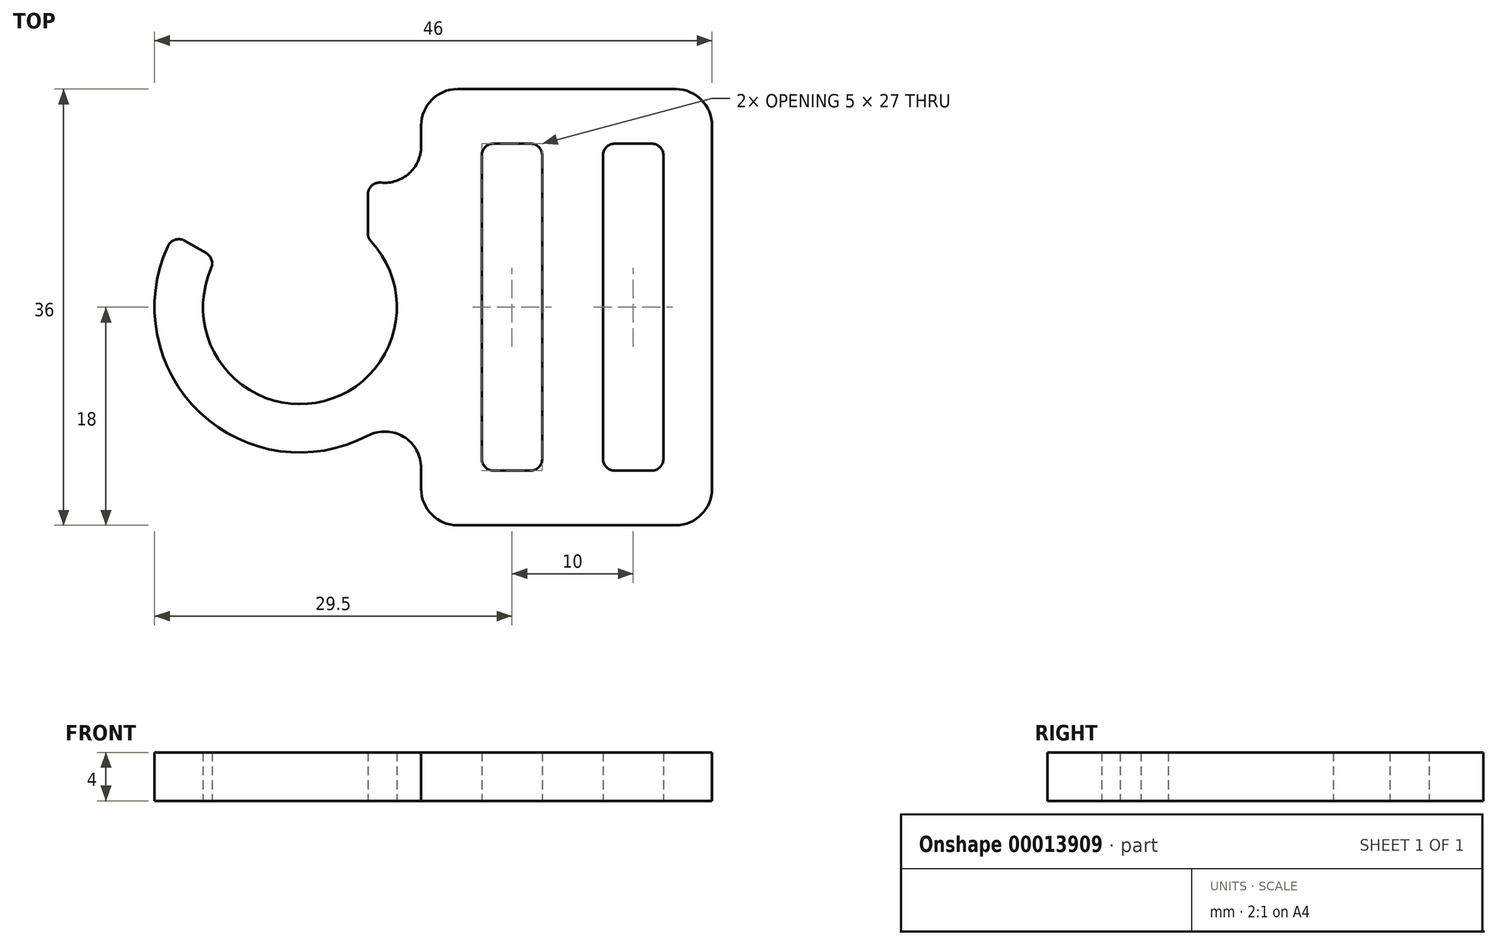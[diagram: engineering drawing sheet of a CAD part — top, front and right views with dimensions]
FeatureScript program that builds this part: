
annotation { "Feature Type Name" : "Feature", "Feature Type Description" : "" }
export const myFeature = defineFeature(function(context is Context, id is Id, definition is map)
    precondition{}
    {
        {
            var Q0;
            Q0=qCreatedBy(makeId("Top.planeOp"),FACE);
            var sketch = newSketch(context, id + "F0", { "sketchPlane" : qUnion([Q0])});
            skArc(sketch, "E0", {"start": v(-10.9, 5.03) * mm, "mid": v(-8.26, -8.7) * mm, "end": v(5.6, -10.61) * mm});
            skLineSegment(sketch, "E1.bottom", {"start": v(13, 18) * mm, "end": v(31, 18) * mm});
            skLineSegment(sketch, "E1.top", {"start": v(13, -18) * mm, "end": v(31, -18) * mm});
            skLineSegment(sketch, "E1.left", {"start": v(10, 15) * mm, "end": v(10, 13.27) * mm});
            skLineSegment(sketch, "E1.right", {"start": v(34, 15) * mm, "end": v(34, -15) * mm});
            skArc(sketch, "E2", {"start": v(-7.33, 3.2) * mm, "mid": v(1.34, -7.89) * mm, "end": v(5.87, 5.44) * mm});
            skLineSegment(sketch, "E3.trimOffspring", {"start": v(10, -13.27) * mm, "end": v(10, -15) * mm});
            skLineSegment(sketch, "E4.bottom", {"start": v(16, 13.5) * mm, "end": v(19, 13.5) * mm});
            skLineSegment(sketch, "E4.top", {"start": v(16, -13.5) * mm, "end": v(19, -13.5) * mm});
            skLineSegment(sketch, "E4.left", {"start": v(15, 12.5) * mm, "end": v(15, -12.5) * mm});
            skLineSegment(sketch, "E4.right", {"start": v(20, 12.5) * mm, "end": v(20, -12.5) * mm});
            skLineSegment(sketch, "E5.bottom", {"start": v(26, 13.5) * mm, "end": v(29, 13.5) * mm});
            skLineSegment(sketch, "E5.top", {"start": v(26, -13.5) * mm, "end": v(29, -13.5) * mm});
            skLineSegment(sketch, "E5.left", {"start": v(25, 12.5) * mm, "end": v(25, -12.5) * mm});
            skLineSegment(sketch, "E5.right", {"start": v(30, 12.5) * mm, "end": v(30, -12.5) * mm});
            skLineSegment(sketch, "E6", {"start": v(0, 0) * mm, "end": v(34, 0) * mm, "construction": true});
            skPoint(sketch, "E7", {"position": v(25, 0) * mm});
            skPoint(sketch, "E8.visualSharp", {"position": v(10, 6.63) * mm});
            skArc(sketch, "E8.filletArc", {"start": v(6.7, 10.28) * mm, "mid": v(9.01, 11.04) * mm, "end": v(10, 13.27) * mm});
            skPoint(sketch, "E9.visualSharp", {"position": v(10, -6.63) * mm});
            skArc(sketch, "E9.filletArc", {"start": v(10, -13.27) * mm, "mid": v(8.55, -10.7) * mm, "end": v(5.6, -10.61) * mm});
            skPoint(sketch, "E10.visualSharp", {"position": v(10, -18) * mm});
            skArc(sketch, "E10.filletArc", {"start": v(10, -15) * mm, "mid": v(10.88, -17.12) * mm, "end": v(13, -18) * mm});
            skPoint(sketch, "E11.visualSharp", {"position": v(34, -18) * mm});
            skArc(sketch, "E11.filletArc", {"start": v(31, -18) * mm, "mid": v(33.12, -17.12) * mm, "end": v(34, -15) * mm});
            skPoint(sketch, "E12.visualSharp", {"position": v(34, 18) * mm});
            skArc(sketch, "E12.filletArc", {"start": v(34, 15) * mm, "mid": v(33.12, 17.12) * mm, "end": v(31, 18) * mm});
            skPoint(sketch, "E13.visualSharp", {"position": v(10, 18) * mm});
            skArc(sketch, "E13.filletArc", {"start": v(13, 18) * mm, "mid": v(10.88, 17.12) * mm, "end": v(10, 15) * mm});
            skPoint(sketch, "E14.visualSharp", {"position": v(15, 13.5) * mm});
            skArc(sketch, "E14.filletArc", {"start": v(16, 13.5) * mm, "mid": v(15.3, 13.2) * mm, "end": v(15, 12.5) * mm});
            skPoint(sketch, "E15.visualSharp", {"position": v(20, 13.5) * mm});
            skArc(sketch, "E15.filletArc", {"start": v(20, 12.5) * mm, "mid": v(19.7, 13.2) * mm, "end": v(19, 13.5) * mm});
            skPoint(sketch, "E16.visualSharp", {"position": v(25, 13.5) * mm});
            skArc(sketch, "E16.filletArc", {"start": v(26, 13.5) * mm, "mid": v(25.3, 13.2) * mm, "end": v(25, 12.5) * mm});
            skPoint(sketch, "E17.visualSharp", {"position": v(30, 13.5) * mm});
            skArc(sketch, "E17.filletArc", {"start": v(30, 12.5) * mm, "mid": v(29.7, 13.2) * mm, "end": v(29, 13.5) * mm});
            skPoint(sketch, "E18.visualSharp", {"position": v(30, -13.5) * mm});
            skArc(sketch, "E18.filletArc", {"start": v(29, -13.5) * mm, "mid": v(29.7, -13.2) * mm, "end": v(30, -12.5) * mm});
            skPoint(sketch, "E19.visualSharp", {"position": v(25, -13.5) * mm});
            skArc(sketch, "E19.filletArc", {"start": v(25, -12.5) * mm, "mid": v(25.3, -13.2) * mm, "end": v(26, -13.5) * mm});
            skPoint(sketch, "E20.visualSharp", {"position": v(15, -13.5) * mm});
            skArc(sketch, "E20.filletArc", {"start": v(15, -12.5) * mm, "mid": v(15.3, -13.2) * mm, "end": v(16, -13.5) * mm});
            skPoint(sketch, "E21.visualSharp", {"position": v(20, -13.5) * mm});
            skArc(sketch, "E21.filletArc", {"start": v(19, -13.5) * mm, "mid": v(19.7, -13.2) * mm, "end": v(20, -12.5) * mm});
            skLineSegment(sketch, "E22", {"start": v(5.6, 9.29) * mm, "end": v(5.6, 6.12) * mm});
            skLineSegment(sketch, "E23", {"start": v(-9.49, 5.48) * mm, "end": v(-7.75, 4.47) * mm});
            skPoint(sketch, "E24.visualSharp", {"position": v(-10.4, 6) * mm});
            skArc(sketch, "E24.filletArc", {"start": v(-9.49, 5.48) * mm, "mid": v(-10.29, 5.56) * mm, "end": v(-10.9, 5.03) * mm});
            skPoint(sketch, "E25.visualSharp", {"position": v(-6.93, 4) * mm});
            skArc(sketch, "E25.filletArc", {"start": v(-7.33, 3.2) * mm, "mid": v(-7.3, 3.92) * mm, "end": v(-7.75, 4.47) * mm});
            skPoint(sketch, "E26.visualSharp", {"position": v(5.6, 5.71) * mm});
            skArc(sketch, "E26.filletArc", {"start": v(5.6, 6.12) * mm, "mid": v(5.67, 5.75) * mm, "end": v(5.87, 5.44) * mm});
            skPoint(sketch, "E27.visualSharp", {"position": v(5.6, 10.61) * mm});
            skArc(sketch, "E27.filletArc", {"start": v(6.7, 10.28) * mm, "mid": v(5.93, 10.03) * mm, "end": v(5.6, 9.29) * mm});
            skSolve(sketch);
        }
        {
            var Q0;
            Q0=qSketchRegion(id+"F0",true);
            extrude(context, id + "F1", {"entities" : qUnion([Q0]), "depth" : 4 * mm});
        }
    });
